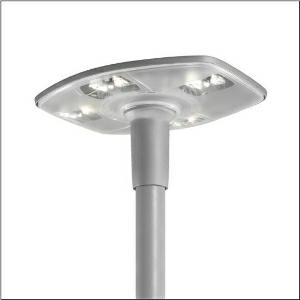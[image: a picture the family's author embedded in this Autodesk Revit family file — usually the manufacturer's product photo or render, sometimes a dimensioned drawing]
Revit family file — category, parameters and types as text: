
# Revit family: dl_30_led___st1_2c_5xa513271b08a5_d9bb
name_source: partatom
category: Lighting Fixtures
units: mm (PartAtom-declared; Revit-internal decimal feet)

## family parameters
Cut with Voids When Loaded = No
Host = Face
Light Source = No
Part Type = Normal
Room Calculation Point = No
Round Connector Dimension = Use Diameter
Shared = No

## types (1)
- --- (1 x LED, 5540 lm, 48.9 W, 4000K)
    Apparent Load = 49 VA
    CIE Flux Codes = 32 71 98 100 100
    Color Rendering = 70
    Color Temperature = 4000K
    Default Elevation = 1800 mm
    Description = DL 30 LED, mast luminaire, primary light control with 3 zone facetted reflector, of plastic, aluminium vaporised, highly specular, primary optical cover: cover, of PMMA, structured, transparent, light distribution: ST1.2c, light emission: direct distribution, primary light characteristic: asymmetric, crossroads, installation type: post-top, LED, High Power LED, rated luminous flux: 5.540lm, luminous efficacy: 113lm/W, light colour: 740, colour temperature: 4000K, control gear: Plus, control: flexible luminous flux parameterisation, time-dependent luminous flux control, constant luminous flux control, digital communication interface, power reduction, electronic power reduction, mains connection: 230..240V, AC, 50/60Hz, start of lifetime: 49W, end of service life: 51W, reduction: 23W, luminaire housing, of diecast aluminium, powder-coated, SITECO metallic grey (DB 702S), length: 600mm, width: 510mm, height: 290mm, spigot size: d x l = 76 x 100mm (post-top) | with reducer (optional accessory) 60 x 100mm, mounting height: 3..6m, protection rating (complete): IP66, insulation class (complete): insulation class II (safety insulation), certification: CE, ENEC, VDE, impact resistance: IK08, permissible operating ambient temperature: -25..+30°C, standard-compliant lighting for roads and squares, packaging unit: 1 piece

Light Distribution: ST1.2c
    Height = 290 mm
    Lamp = 1 x LED
    Lamp Light Flux = 5540 lm
    Lamp Power = 48.9 W
    Lamp count = 1
    Length = 510 mm
    Luminous efficacy = 113 lm/W
    Manufacturer = Siteco
    ModVariant = No
    Model = 5XA513271B08A5
    Number of Poles = 1
    OnlyDefault = Yes
    Power Factor = 1
    Product Name = DL 30 LED | ST1.2c
    Product group = mast luminaire | pylon top
    ProductGroupID = 6100
    Protection Class = Protection class II
    Protection Degree = IP 66
    RLX_Detail_Level = 1
    RLX_Emergency_Light_Flux = 0 lm
    RLX_Emergency_Type = 0
    RLX_Emergency_Type_DB = No
    RlxData = <blob elided: 86473 chars, md5=cf84dc40>
    Socket = socket
    Standby Power = 0 W
    System Light Flux = 5540 lm
    System Power = 49 W
    Type Comments = factory setting: luminous flux: 100 % | dim-lin: 254 | 497 mA
    Type Image = l_1006003.jpg
    URL = http://relux.com
    VarID = @adj_195357
    Voltage = 0 V
    Weight = 0.00 kg
    Width = 600 mm

## geometry (parser evidence)
native form markers: Blend x4, Sweep x11
no freeform markers — native parametric forms only
